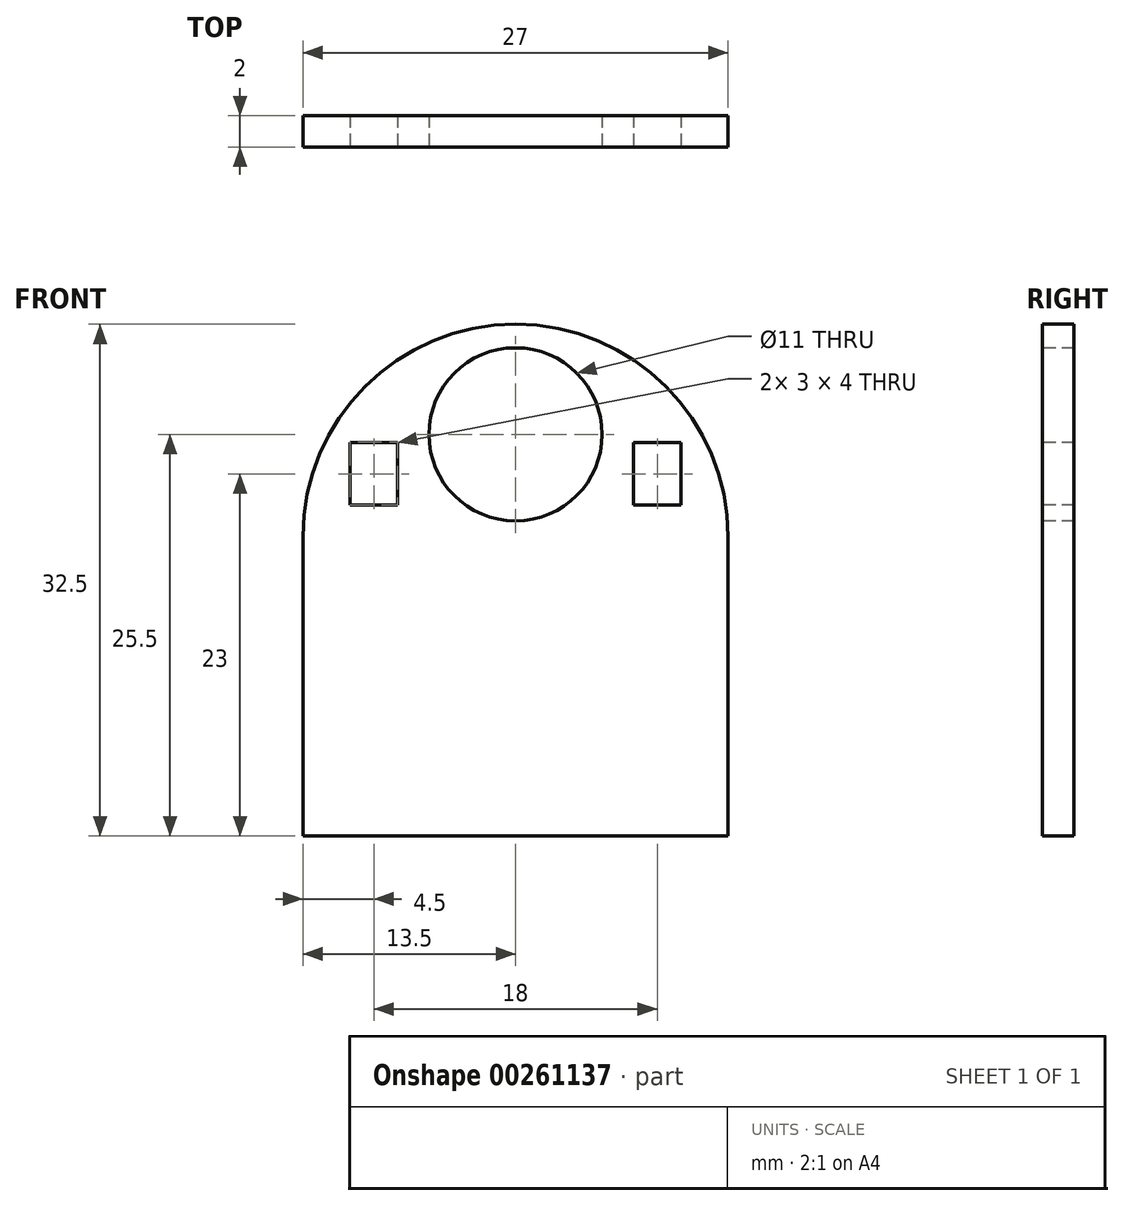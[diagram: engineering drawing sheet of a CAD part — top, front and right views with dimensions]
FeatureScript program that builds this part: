
annotation { "Feature Type Name" : "Feature", "Feature Type Description" : "" }
export const myFeature = defineFeature(function(context is Context, id is Id, definition is map)
    precondition{}
    {
        {
            var Q0;
            Q0=qCreatedBy(makeId("Front.planeOp"),FACE);
            var sketch = newSketch(context, id + "F0", { "sketchPlane" : qUnion([Q0])});
            skCircle(sketch, "E0", {"center": v(0, 0) * mm, "radius": 13.5 * mm});
            skLineSegment(sketch, "E1", {"start": v(-13.5, 0) * mm, "end": v(-13.5, -19) * mm});
            skLineSegment(sketch, "E2", {"start": v(-13.5, -19) * mm, "end": v(13.5, -19) * mm});
            skLineSegment(sketch, "E3", {"start": v(13.5, -19) * mm, "end": v(13.5, 0) * mm});
            skSolve(sketch);
        }
        {
            var Q0;
            Q0=qSketchRegion(id+"F0",true);
            extrude(context, id + "F1", {"entities" : qUnion([Q0]), "depth" : 2 * mm});
        }
        {
            var Q0;
            Q0=makeQuery(id+"F1.opExtrude","CAP_FACE",FACE,{"disambiguationData":[OSD([sQuery(id+"F0.wireOp",EDGE,"E0"),sQuery(id+"F0.wireOp",EDGE,"E1"),sQuery(id+"F0.wireOp",EDGE,"E2"),sQuery(id+"F0.wireOp",EDGE,"E3")])],"isStart":false});
            var sketch = newSketch(context, id + "F2", { "sketchPlane" : qUnion([Q0])});
            skCircle(sketch, "E4", {"center": v(0, 6.5) * mm, "radius": 5.5 * mm});
            skLineSegment(sketch, "E5.bottom", {"start": v(-10.5, 2) * mm, "end": v(-7.5, 2) * mm});
            skLineSegment(sketch, "E5.top", {"start": v(-10.5, 6) * mm, "end": v(-7.5, 6) * mm});
            skLineSegment(sketch, "E5.left", {"start": v(-10.5, 2) * mm, "end": v(-10.5, 6) * mm});
            skLineSegment(sketch, "E5.right", {"start": v(-7.5, 2) * mm, "end": v(-7.5, 6) * mm});
            skLineSegment(sketch, "E6.bottom", {"start": v(7.5, 6) * mm, "end": v(10.5, 6) * mm});
            skLineSegment(sketch, "E6.top", {"start": v(7.5, 2) * mm, "end": v(10.5, 2) * mm});
            skLineSegment(sketch, "E6.left", {"start": v(7.5, 6) * mm, "end": v(7.5, 2) * mm});
            skLineSegment(sketch, "E6.right", {"start": v(10.5, 6) * mm, "end": v(10.5, 2) * mm});
            skSolve(sketch);
        }
        {
            var Q0;
            Q0 = qSketchRegion(id + "F2", true);
            extrude(context, id + "F3", {"entities" : qUnion([Q0]), "operationType" : NewBodyOperationType.REMOVE, "oppositeDirection" : true, "depth" : 2 * mm});
        }
    });
